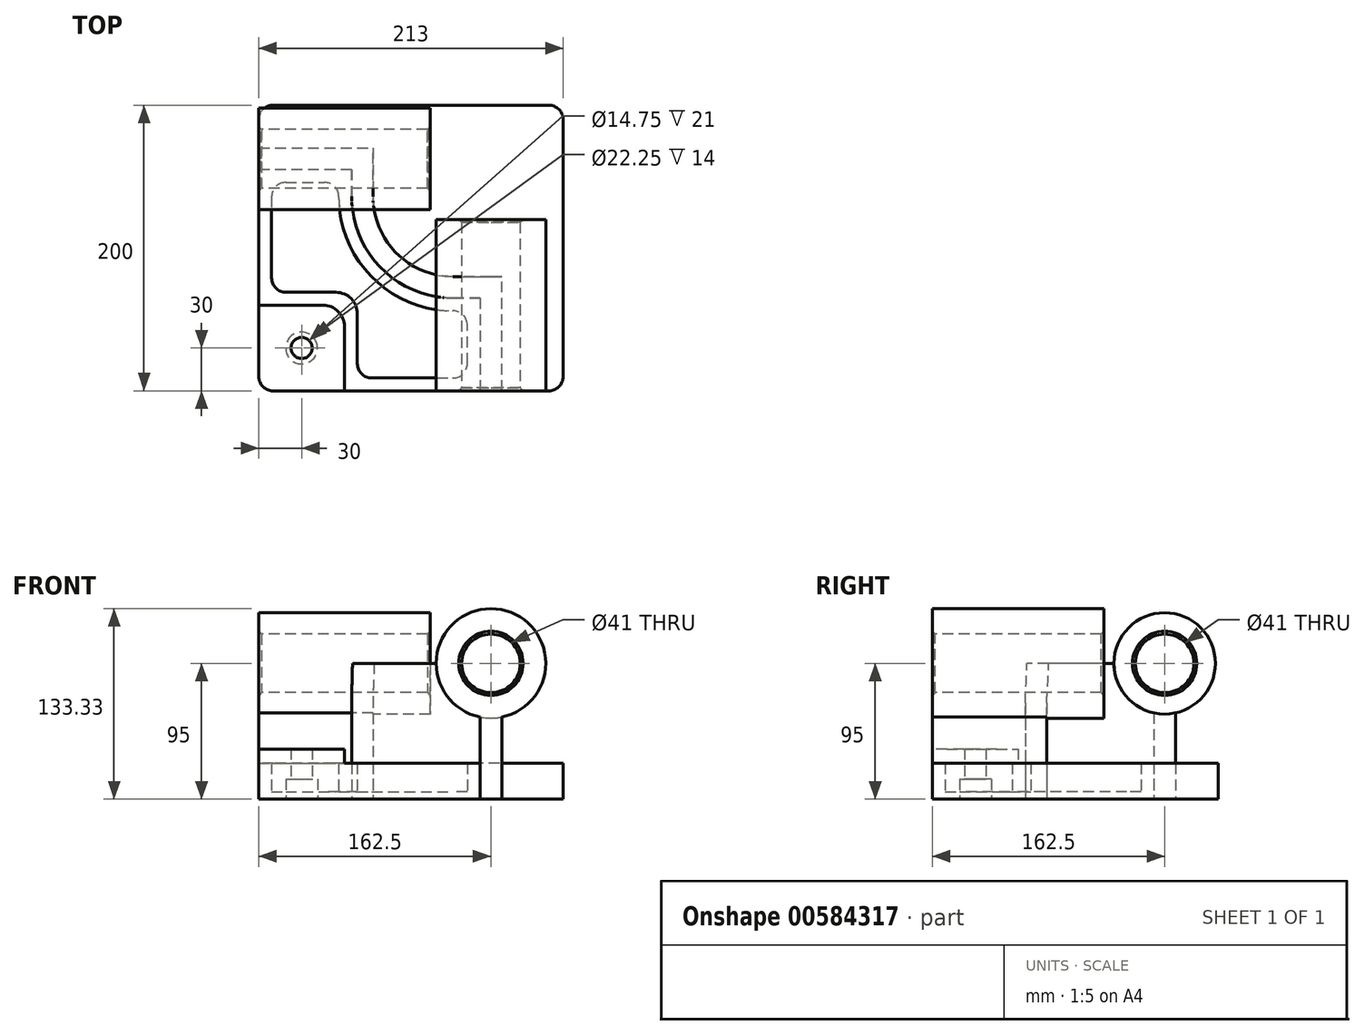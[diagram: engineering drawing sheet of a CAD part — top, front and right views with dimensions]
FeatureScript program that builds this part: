
annotation { "Feature Type Name" : "Feature", "Feature Type Description" : "" }
export const myFeature = defineFeature(function(context is Context, id is Id, definition is map)
    precondition{}
    {
        {
            var Q0;
            Q0=qCreatedBy(makeId("Top.planeOp"),FACE);
            var sketch = newSketch(context, id + "F0", { "sketchPlane" : qUnion([Q0])});
            skLineSegment(sketch, "E0.bottom", {"start": v(96.5, -100) * mm, "end": v(-96.5, -100) * mm});
            skLineSegment(sketch, "E0.top", {"start": v(96.5, 100) * mm, "end": v(-96.5, 100) * mm});
            skLineSegment(sketch, "E0.left", {"start": v(106.5, -90) * mm, "end": v(106.5, 90) * mm});
            skLineSegment(sketch, "E0.right", {"start": v(-106.5, -90) * mm, "end": v(-106.5, 90) * mm});
            skPoint(sketch, "E0.middle", {"position": v(0, 0) * mm});
            skPoint(sketch, "E1.visualSharp", {"position": v(-106.5, 100) * mm});
            skArc(sketch, "E1.filletArc", {"start": v(-96.5, 100) * mm, "mid": v(-103.57, 97.07) * mm, "end": v(-106.5, 90) * mm});
            skPoint(sketch, "E2.visualSharp", {"position": v(106.5, 100) * mm});
            skArc(sketch, "E2.filletArc", {"start": v(106.5, 90) * mm, "mid": v(103.57, 97.07) * mm, "end": v(96.5, 100) * mm});
            skPoint(sketch, "E3.visualSharp", {"position": v(106.5, -100) * mm});
            skArc(sketch, "E3.filletArc", {"start": v(96.5, -100) * mm, "mid": v(103.57, -97.07) * mm, "end": v(106.5, -90) * mm});
            skPoint(sketch, "E4.visualSharp", {"position": v(-106.5, -100) * mm});
            skArc(sketch, "E4.filletArc", {"start": v(-106.5, -90) * mm, "mid": v(-103.57, -97.07) * mm, "end": v(-96.5, -100) * mm});
            skLineSegment(sketch, "E5", {"start": v(-106.5, -40) * mm, "end": v(-61.5, -40) * mm});
            skLineSegment(sketch, "E6", {"start": v(-46.5, -55) * mm, "end": v(-46.5, -100) * mm});
            skPoint(sketch, "E7.visualSharp", {"position": v(-46.5, -40) * mm});
            skArc(sketch, "E7.filletArc", {"start": v(-46.5, -55) * mm, "mid": v(-50.9, -44.4) * mm, "end": v(-61.5, -40) * mm});
            skPoint(sketch, "E8", {"position": v(-76.5, -70) * mm});
            skLineSegment(sketch, "E9", {"start": v(-106.5, 0) * mm, "end": v(-97.5, 0) * mm, "construction": true});
            skPoint(sketch, "E9.endSnap0", {"position": v(-106.5, 0) * mm});
            skLineSegment(sketch, "E10", {"start": v(-84, -40) * mm, "end": v(-84, -31) * mm, "construction": true});
            skLineSegment(sketch, "E11", {"start": v(-46.5, -77.5) * mm, "end": v(-37.5, -77.5) * mm, "construction": true});
            skLineSegment(sketch, "E12", {"start": v(0, -100) * mm, "end": v(0, -91) * mm, "construction": true});
            skPoint(sketch, "E13", {"position": v(-97.5, 46) * mm});
            skLineSegment(sketch, "E14", {"start": v(-97.5, 36) * mm, "end": v(-97.5, -21) * mm});
            skLineSegment(sketch, "E15", {"start": v(-87.5, -31) * mm, "end": v(-52.5, -31) * mm});
            skLineSegment(sketch, "E16", {"start": v(-37.5, -46) * mm, "end": v(-37.5, -81) * mm});
            skPoint(sketch, "E17", {"position": v(39.5, -91) * mm});
            skLineSegment(sketch, "E18", {"start": v(-27.5, -91) * mm, "end": v(29.5, -91) * mm});
            skPoint(sketch, "E19.visualSharp", {"position": v(-37.5, -31) * mm});
            skArc(sketch, "E19.filletArc", {"start": v(-37.5, -46) * mm, "mid": v(-41.9, -35.4) * mm, "end": v(-52.5, -31) * mm});
            skPoint(sketch, "E20", {"position": v(-50.5, 46) * mm});
            skPoint(sketch, "E21", {"position": v(39.5, -44) * mm});
            skLineSegment(sketch, "E22", {"start": v(-87.5, 46) * mm, "end": v(-60.5, 46) * mm});
            skLineSegment(sketch, "E23", {"start": v(39.5, -81) * mm, "end": v(39.5, -54) * mm});
            skLineSegment(sketch, "E24", {"start": v(29.5, -44) * mm, "end": v(29.5, -44) * mm});
            skLineSegment(sketch, "E25", {"start": v(-50.5, 36) * mm, "end": v(-50.5, 36) * mm});
            skArc(sketch, "E26.filletArc", {"start": v(-50.5, 36) * mm, "mid": v(-53.43, 43.07) * mm, "end": v(-60.5, 46) * mm});
            skArc(sketch, "E27.filletArc", {"start": v(-87.5, 46) * mm, "mid": v(-94.57, 43.07) * mm, "end": v(-97.5, 36) * mm});
            skPoint(sketch, "E28.visualSharp", {"position": v(-97.5, -31) * mm});
            skArc(sketch, "E28.filletArc", {"start": v(-97.5, -21) * mm, "mid": v(-94.57, -28.07) * mm, "end": v(-87.5, -31) * mm});
            skPoint(sketch, "E29.visualSharp", {"position": v(-37.5, -91) * mm});
            skArc(sketch, "E29.filletArc", {"start": v(-37.5, -81) * mm, "mid": v(-34.57, -88.07) * mm, "end": v(-27.5, -91) * mm});
            skArc(sketch, "E30.filletArc", {"start": v(29.5, -91) * mm, "mid": v(36.57, -88.07) * mm, "end": v(39.5, -81) * mm});
            skArc(sketch, "E31.filletArc", {"start": v(39.5, -54) * mm, "mid": v(36.57, -46.93) * mm, "end": v(29.5, -44) * mm});
            skPoint(sketch, "E32.visualSharp", {"position": v(-50.5, -44) * mm});
            skArc(sketch, "E32.filletArc", {"start": v(-50.5, 36) * mm, "mid": v(-27.07, -20.57) * mm, "end": v(29.5, -44) * mm});
            skPoint(sketch, "E33", {"position": v(-106.5, 55) * mm});
            skPoint(sketch, "E34", {"position": v(-106.5, 70) * mm});
            skPoint(sketch, "E35", {"position": v(48.5, -100) * mm});
            skPoint(sketch, "E36", {"position": v(63.5, -100) * mm});
            skPoint(sketch, "E37", {"position": v(-26.5, 70) * mm});
            skPoint(sketch, "E38", {"position": v(63.5, -20) * mm});
            skPoint(sketch, "E39", {"position": v(-41.5, 55) * mm});
            skPoint(sketch, "E40", {"position": v(48.5, -35) * mm});
            skLineSegment(sketch, "E41", {"start": v(-106.5, 55) * mm, "end": v(-41.5, 55) * mm});
            skLineSegment(sketch, "E42", {"start": v(-106.5, 70) * mm, "end": v(-26.5, 70) * mm});
            skLineSegment(sketch, "E43", {"start": v(63.5, -100) * mm, "end": v(63.5, -20) * mm});
            skLineSegment(sketch, "E44", {"start": v(48.5, -100) * mm, "end": v(48.5, -35) * mm});
            skLineSegment(sketch, "E45", {"start": v(-41.5, 55) * mm, "end": v(-41.5, 36) * mm});
            skLineSegment(sketch, "E46", {"start": v(29.5, -35) * mm, "end": v(48.5, -35) * mm});
            skPoint(sketch, "E47.visualSharp", {"position": v(-41.5, -35) * mm});
            skArc(sketch, "E47.filletArc", {"start": v(-41.5, 36) * mm, "mid": v(-20.7, -14.2) * mm, "end": v(29.5, -35) * mm});
            skLineSegment(sketch, "E48", {"start": v(-26.5, 70) * mm, "end": v(-26.5, 36) * mm});
            skLineSegment(sketch, "E49", {"start": v(29.5, -20) * mm, "end": v(63.5, -20) * mm});
            skPoint(sketch, "E50.visualSharp", {"position": v(-26.5, -20) * mm});
            skArc(sketch, "E50.filletArc", {"start": v(-26.5, 36) * mm, "mid": v(-10.1, -3.6) * mm, "end": v(29.5, -20) * mm});
            skSolve(sketch);
        }
        {
            var Q0;
            {var subQ1=sQuery(id+"F0.wireOp",EDGE,"E4.filletArc");Q0=makeQuery(id+"F0.imprint","IMPRINT",FACE,{"disambiguationData":[TD([[makeQuery(id+"F0.imprint","IMPRINT",EDGE,{"derivedFrom":subQ1}),1.0]])]});}
            extrude(context, id + "F1", {"entities" : qUnion([Q0]), "depth" : 35 * mm, "offsetDistance" : 25 * mm});
        }
        {
            var Q0;
            {var subQ3=sQuery(id+"F0.wireOp",EDGE,"E5");Q0=makeQuery(id+"F0.imprint","IMPRINT",FACE,{"disambiguationData":[TD([[makeQuery(id+"F0.imprint","IMPRINT",EDGE,{"derivedFrom":subQ3}),1.0]])]});}
            var Q1;
            Q1=makeQuery(id+"F0.imprint","IMPRINT",FACE,{"disambiguationData":[TD([[makeQuery(id+"F0.imprint","IMPRINT",EDGE,{"derivedFrom":sQuery(id+"F0.wireOp",EDGE,"E0.top")}),1.0]])]});
            extrude(context, id + "F2", {"entities" : qUnion([Q0, Q1]), "operationType" : NewBodyOperationType.ADD, "depth" : 25 * mm, "offsetDistance" : 25 * mm});
        }
        {
            var Q0;
            {var subQ3=sQuery(id+"F0.wireOp",EDGE,"E41");Q0=makeQuery(id+"F0.imprint","IMPRINT",FACE,{"disambiguationData":[TD([[makeQuery(id+"F0.imprint","IMPRINT",EDGE,{"derivedFrom":subQ3}),1.0]])]});}
            extrude(context, id + "F3", {"entities" : qUnion([Q0]), "depth" : 95 * mm, "offsetDistance" : 25 * mm});
        }
        {
            var Q0;
            Q0=makeQuery(id+"F0.imprint","IMPRINT",FACE,{"disambiguationData":[TD([[makeQuery(id+"F0.imprint","IMPRINT",EDGE,{"derivedFrom":sQuery(id+"F0.wireOp",EDGE,"E14")}),1.0]])]});
            extrude(context, id + "F4", {"entities" : qUnion([Q0]), "operationType" : NewBodyOperationType.ADD, "depth" : 5 * mm, "offsetDistance" : 25 * mm});
        }
        {
            var Q0;
            Q0=sQuery(id+"F0.wireOp",VERTEX,"E8");
            var Q1;
            Q1=makeQuery(id+"F1.opExtrude","SWEPT_BODY",BODY,{"disambiguationData":[OSD([sQuery(id+"F0.wireOp",EDGE,"E0.bottom"),sQuery(id+"F0.wireOp",EDGE,"E0.right"),sQuery(id+"F0.wireOp",EDGE,"E4.filletArc"),sQuery(id+"F0.wireOp",EDGE,"E5"),sQuery(id+"F0.wireOp",EDGE,"E6"),sQuery(id+"F0.wireOp",EDGE,"E7.filletArc")])]});
            hole(context, id + "F5", {"style" : HoleStyle.C_BORE, "endStyle" : HoleEndStyle.THROUGH, "oppositeDirection" : true, "standardTappedOrClearance" : lookupTablePath({ "standard" : "ISO", "fit" : "Close", "size" : "M14", "type" : "Clearance" }), "standardBlindInLast" : lookupTablePath({ "fit" : "Close", "standard" : "ISO", "size" : "M14", "type" : "Clearance" }), "holeDiameter" : 14.75 * mm, "cBoreDiameter" : 22.25 * mm, "cBoreDepth" : 14 * mm, "majorDiameter" : 5 * mm, "isTappedThrough" : true, "tappedDepth" : 12 * mm, "tapClearance" : 3, "locations" : qUnion([Q0]), "scope" : qUnion([Q1])});
        }
        {
            var Q0;
            Q0=makeQuery(id+"F3.opExtrude","SWEPT_FACE",FACE,{"disambiguationData":[OSD([sQuery(id+"F0.wireOp",EDGE,"E0.bottom")])]});
            var sketch = newSketch(context, id + "F6", { "sketchPlane" : qUnion([Q0])});
            skLineSegment(sketch, "E51.0", {"start": v(63.5, 95) * mm, "end": v(48.5, 95) * mm});
            skCircle(sketch, "E52", {"center": v(56, 95) * mm, "radius": 20.5 * mm});
            skCircle(sketch, "E53", {"center": v(56, 95) * mm, "radius": 38.33 * mm});
            skSolve(sketch);
        }
        {
            var Q0;
            {var subQ0=sQuery(id+"F6.wireOp",EDGE,"E51.0");Q0=makeQuery(id+"F6.imprint","IMPRINT",FACE,{"disambiguationData":[TD([[makeQuery(id+"F6.imprint","IMPRINT",EDGE,{"derivedFrom":subQ0}),1.0]])]});}
            var Q1;
            {var subQ0=sQuery(id+"F6.wireOp",EDGE,"E51.0");Q1=makeQuery(id+"F6.imprint","IMPRINT",FACE,{"disambiguationData":[TD([[makeQuery(id+"F6.imprint","IMPRINT",EDGE,{"derivedFrom":subQ0}),-1.0]])]});}
            extrude(context, id + "F7", {"entities" : qUnion([Q0, Q1]), "operationType" : NewBodyOperationType.REMOVE, "oppositeDirection" : true, "depth" : 120 * mm, "offsetDistance" : 25 * mm});
        }
        {
            var Q0;
            {var subQ0=sQuery(id+"F6.wireOp",EDGE,"E52");var subQ1=sQuery(id+"F0.wireOp",EDGE,"E0.bottom");var subQ2=makeQuery(id+"F3.opExtrude","SWEPT_EDGE",EDGE,{"disambiguationData":[OSD([subQ1,sQuery(id+"F0.wireOp",EDGE,"E43")])]});var subQ3=makeQuery(id+"F6.imprint","INTERSECT",VERTEX,{"derivedFrom":[subQ2,subQ0]});Q0=makeQuery(id+"F6.imprint","IMPRINT",FACE,{"disambiguationData":[TD([[makeQuery(id+"F6.imprint","IMPRINT",EDGE,{"disambiguationData":[TD([[subQ3,-1.0]])],"derivedFrom":subQ0}),-1.0]])]});}
            var Q1;
            {var subQ0=sQuery(id+"F6.wireOp",EDGE,"E52");var subQ1=sQuery(id+"F0.wireOp",EDGE,"E0.bottom");var subQ2=makeQuery(id+"F3.opExtrude","SWEPT_EDGE",EDGE,{"disambiguationData":[OSD([subQ1,sQuery(id+"F0.wireOp",EDGE,"E43")])]});var subQ3=makeQuery(id+"F6.imprint","INTERSECT",VERTEX,{"derivedFrom":[subQ2,subQ0]});Q1=makeQuery(id+"F6.imprint","IMPRINT",FACE,{"disambiguationData":[TD([[makeQuery(id+"F6.imprint","IMPRINT",EDGE,{"disambiguationData":[TD([[subQ3,1.0]])],"derivedFrom":subQ0}),-1.0]])]});}
            extrude(context, id + "F8", {"entities" : qUnion([Q0, Q1]), "operationType" : NewBodyOperationType.ADD, "oppositeDirection" : true, "depth" : 120 * mm, "offsetDistance" : 25 * mm});
        }
        {
            var Q0;
            Q0=makeQuery(id+"F3.opExtrude","SWEPT_FACE",FACE,{"disambiguationData":[OSD([sQuery(id+"F0.wireOp",EDGE,"E0.right")])]});
            var sketch = newSketch(context, id + "F9", { "sketchPlane" : qUnion([Q0])});
            skLineSegment(sketch, "E54.0", {"start": v(-55, 95) * mm, "end": v(-70, 95) * mm});
            skCircle(sketch, "E55", {"center": v(-62.5, 95) * mm, "radius": 20.5 * mm});
            skCircle(sketch, "E56", {"center": v(-62.5, 95) * mm, "radius": 35.5 * mm});
            skSolve(sketch);
        }
        {
            var Q0;
            {var subQ0=sQuery(id+"F9.wireOp",EDGE,"E54.0");Q0=makeQuery(id+"F9.imprint","IMPRINT",FACE,{"disambiguationData":[TD([[makeQuery(id+"F9.imprint","IMPRINT",EDGE,{"derivedFrom":subQ0}),1.0]])]});}
            var Q1;
            {var subQ0=sQuery(id+"F9.wireOp",EDGE,"E54.0");Q1=makeQuery(id+"F9.imprint","IMPRINT",FACE,{"disambiguationData":[TD([[makeQuery(id+"F9.imprint","IMPRINT",EDGE,{"derivedFrom":subQ0}),-1.0]])]});}
            extrude(context, id + "F10", {"entities" : qUnion([Q0, Q1]), "operationType" : NewBodyOperationType.REMOVE, "oppositeDirection" : true, "depth" : 120 * mm, "offsetDistance" : 25 * mm});
        }
        {
            var Q0;
            {var subQ0=sQuery(id+"F9.wireOp",EDGE,"E55");var subQ1=sQuery(id+"F0.wireOp",EDGE,"E0.right");var subQ2=makeQuery(id+"F3.opExtrude","SWEPT_EDGE",EDGE,{"disambiguationData":[OSD([subQ1,sQuery(id+"F0.wireOp",EDGE,"E41")])]});var subQ3=makeQuery(id+"F9.imprint","INTERSECT",VERTEX,{"derivedFrom":[subQ2,subQ0]});Q0=makeQuery(id+"F9.imprint","IMPRINT",FACE,{"disambiguationData":[TD([[makeQuery(id+"F9.imprint","IMPRINT",EDGE,{"disambiguationData":[TD([[subQ3,-1.0]])],"derivedFrom":subQ0}),-1.0]])]});}
            var Q1;
            {var subQ0=sQuery(id+"F9.wireOp",EDGE,"E55");var subQ1=sQuery(id+"F0.wireOp",EDGE,"E0.right");var subQ2=makeQuery(id+"F3.opExtrude","SWEPT_EDGE",EDGE,{"disambiguationData":[OSD([subQ1,sQuery(id+"F0.wireOp",EDGE,"E41")])]});var subQ3=makeQuery(id+"F9.imprint","INTERSECT",VERTEX,{"derivedFrom":[subQ2,subQ0]});Q1=makeQuery(id+"F9.imprint","IMPRINT",FACE,{"disambiguationData":[TD([[makeQuery(id+"F9.imprint","IMPRINT",EDGE,{"disambiguationData":[TD([[subQ3,1.0]])],"derivedFrom":subQ0}),-1.0]])]});}
            extrude(context, id + "F11", {"entities" : qUnion([Q0, Q1]), "operationType" : NewBodyOperationType.ADD, "oppositeDirection" : true, "depth" : 120 * mm, "offsetDistance" : 25 * mm});
        }
        {
            var Q0;
            {var subQ0=sQuery(id+"F9.wireOp",EDGE,"E55");Q0=makeQuery(id+"F11.boolean.opBoolean","MERGE",EDGE,{"derivedFrom":[makeQuery(id+"F10.boolean.opBoolean","COPY",EDGE,{"derivedFrom":makeQuery(id+"F10.opExtrude","CAP_EDGE",EDGE,{"disambiguationData":[OSD([subQ0])],"isStart":true})}),makeQuery(id+"F11.opExtrude","CAP_EDGE",EDGE,{"disambiguationData":[OSD([subQ0])],"isStart":true})]});}
            var Q1;
            Q1=makeQuery(id+"F11.opExtrude","CAP_EDGE",EDGE,{"disambiguationData":[OSD([sQuery(id+"F9.wireOp",EDGE,"E55")])],"isStart":false});
            var Q2;
            Q2=makeQuery(id+"F8.opExtrude","CAP_EDGE",EDGE,{"disambiguationData":[OSD([sQuery(id+"F6.wireOp",EDGE,"E52")])],"isStart":false});
            var Q3;
            {var subQ0=sQuery(id+"F6.wireOp",EDGE,"E52");Q3=makeQuery(id+"F8.boolean.opBoolean","MERGE",EDGE,{"derivedFrom":[makeQuery(id+"F7.boolean.opBoolean","COPY",EDGE,{"derivedFrom":makeQuery(id+"F7.opExtrude","CAP_EDGE",EDGE,{"disambiguationData":[OSD([subQ0])],"isStart":true})}),makeQuery(id+"F8.opExtrude","CAP_EDGE",EDGE,{"disambiguationData":[OSD([subQ0])],"isStart":true})]});}
            chamfer(context, id + "F12", {"entities" : qUnion([Q0, Q1, Q2, Q3]), "chamferType" : ChamferType.OFFSET_ANGLE, "width" : 2 * mm, "oppositeDirection" : false, "angle" : 45 * degree, "tangentPropagation" : true});
        }
    });
